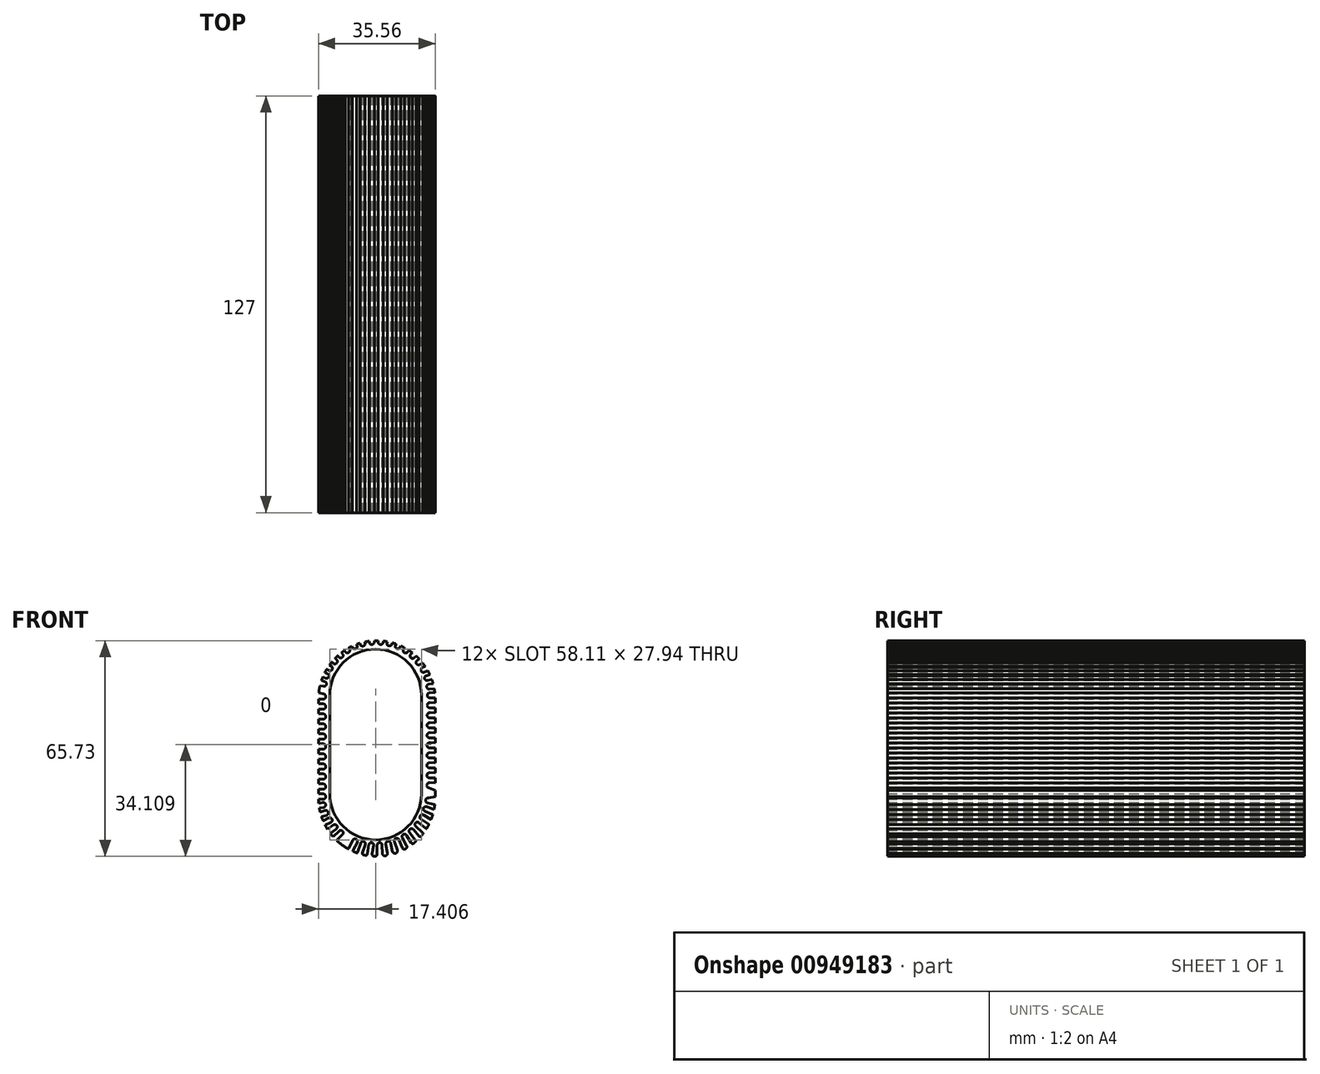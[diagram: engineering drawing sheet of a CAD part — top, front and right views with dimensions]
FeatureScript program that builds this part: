
annotation { "Feature Type Name" : "Feature", "Feature Type Description" : "" }
export const myFeature = defineFeature(function(context is Context, id is Id, definition is map)
    precondition{}
    {
        {
            var Q0;
            Q0=qCreatedBy(makeId("Front.planeOp"),FACE);
            var sketch = newSketch(context, id + "F0", { "sketchPlane" : qUnion([Q0])});
            skLineSegment(sketch, "E0", {"start": v(-13.83, 27.75) * mm, "end": v(-13.83, -2.42) * mm});
            skArc(sketch, "E1", {"start": v(14.1, 27.75) * mm, "mid": v(0.14, 41.72) * mm, "end": v(-13.83, 27.75) * mm});
            skLineSegment(sketch, "E2", {"start": v(14.1, 27.75) * mm, "end": v(14.1, -2.42) * mm});
            skArc(sketch, "E3", {"start": v(-13.83, -2.42) * mm, "mid": v(0.14, -16.39) * mm, "end": v(14.1, -2.42) * mm});
            skLineSegment(sketch, "E4", {"start": v(-0.26, 43.88) * mm, "end": v(-0.26, 46.62) * mm});
            skArc(sketch, "E5", {"start": v(1.27, 46.62) * mm, "mid": v(0.5, 47.38) * mm, "end": v(-0.26, 46.62) * mm});
            skArc(sketch, "E6", {"start": v(-1.78, 43.88) * mm, "mid": v(-1.02, 43.11) * mm, "end": v(-0.26, 43.88) * mm});
            skLineSegment(sketch, "E7", {"start": v(10.26, 54.84) * mm, "end": v(11.29, 54.45) * mm});
            skLineSegment(sketch, "E8", {"start": v(15.28, 62.77) * mm, "end": v(24.92, 59.85) * mm});
            skLineSegment(sketch, "E9", {"start": v(27, 48.57) * mm, "end": v(25.56, 56.37) * mm});
            skLineSegment(sketch, "E10", {"start": v(25.56, 56.37) * mm, "end": v(8.9, 53.3) * mm});
            skLineSegment(sketch, "E11", {"start": v(15.28, 62.77) * mm, "end": v(24.38, 62.77) * mm});
            skLineSegment(sketch, "E12.trimOffspring", {"start": v(24.92, 59.85) * mm, "end": v(24.38, 62.77) * mm});
            skArc(sketch, "E13.1.0", {"start": v(0.93, 44) * mm, "mid": v(1.56, 43.13) * mm, "end": v(2.43, 43.75) * mm});
            skLineSegment(sketch, "E13.1.1", {"start": v(2.43, 43.75) * mm, "end": v(2.89, 46.46) * mm});
            skArc(sketch, "E13.1.2", {"start": v(4.39, 46.21) * mm, "mid": v(3.76, 47.09) * mm, "end": v(2.89, 46.46) * mm});
            skArc(sketch, "E13.2.0", {"start": v(3.62, 43.69) * mm, "mid": v(4.1, 42.72) * mm, "end": v(5.07, 43.2) * mm});
            skLineSegment(sketch, "E13.2.1", {"start": v(5.07, 43.2) * mm, "end": v(5.96, 45.79) * mm});
            skArc(sketch, "E13.2.2", {"start": v(7.4, 45.3) * mm, "mid": v(6.92, 46.26) * mm, "end": v(5.96, 45.79) * mm});
            skArc(sketch, "E13.3.0", {"start": v(6.23, 42.93) * mm, "mid": v(6.54, 41.9) * mm, "end": v(7.57, 42.2) * mm});
            skLineSegment(sketch, "E13.3.1", {"start": v(7.57, 42.2) * mm, "end": v(8.88, 44.62) * mm});
            skArc(sketch, "E13.3.2", {"start": v(10.22, 43.9) * mm, "mid": v(9.9, 44.93) * mm, "end": v(8.88, 44.62) * mm});
            skArc(sketch, "E13.4.0", {"start": v(8.67, 41.75) * mm, "mid": v(8.8, 40.68) * mm, "end": v(9.87, 40.82) * mm});
            skLineSegment(sketch, "E13.4.1", {"start": v(9.87, 40.82) * mm, "end": v(11.56, 42.98) * mm});
            skArc(sketch, "E13.4.2", {"start": v(12.76, 42.05) * mm, "mid": v(12.63, 43.12) * mm, "end": v(11.56, 42.98) * mm});
            skArc(sketch, "E13.5.0", {"start": v(10.89, 40.19) * mm, "mid": v(10.84, 39.11) * mm, "end": v(11.92, 39.07) * mm});
            skLineSegment(sketch, "E13.5.1", {"start": v(11.92, 39.07) * mm, "end": v(13.94, 40.93) * mm});
            skArc(sketch, "E13.5.2", {"start": v(14.97, 39.8) * mm, "mid": v(15.02, 40.88) * mm, "end": v(13.94, 40.93) * mm});
            skArc(sketch, "E13.6.0", {"start": v(12.82, 38.28) * mm, "mid": v(12.6, 37.23) * mm, "end": v(13.65, 37) * mm});
            skLineSegment(sketch, "E13.6.1", {"start": v(13.65, 37) * mm, "end": v(15.95, 38.5) * mm});
            skArc(sketch, "E13.6.2", {"start": v(16.78, 37.23) * mm, "mid": v(17, 38.29) * mm, "end": v(15.95, 38.5) * mm});
            skArc(sketch, "E13.7.0", {"start": v(14.4, 36.09) * mm, "mid": v(14.02, 35.08) * mm, "end": v(15.02, 34.7) * mm});
            skLineSegment(sketch, "E13.7.1", {"start": v(15.02, 34.7) * mm, "end": v(17.54, 35.8) * mm});
            skArc(sketch, "E13.7.2", {"start": v(18.15, 34.4) * mm, "mid": v(18.54, 35.4) * mm, "end": v(17.54, 35.8) * mm});
            skArc(sketch, "E13.8.0", {"start": v(15.61, 33.66) * mm, "mid": v(15.06, 32.73) * mm, "end": v(15.99, 32.18) * mm});
            skLineSegment(sketch, "E13.8.1", {"start": v(15.99, 32.18) * mm, "end": v(18.65, 32.85) * mm});
            skArc(sketch, "E13.8.2", {"start": v(19.02, 31.38) * mm, "mid": v(19.58, 32.3) * mm, "end": v(18.65, 32.85) * mm});
            skArc(sketch, "E13.9.0", {"start": v(16.4, 31.06) * mm, "mid": v(15.7, 30.24) * mm, "end": v(16.53, 29.54) * mm});
            skLineSegment(sketch, "E13.9.1", {"start": v(16.53, 29.54) * mm, "end": v(19.27, 29.77) * mm});
            skArc(sketch, "E13.9.2", {"start": v(19.35, 28.34) * mm, "mid": v(19.81, 29.08) * mm, "end": v(19.27, 29.77) * mm});
            skArc(sketch, "E13.10.0", {"start": v(16.7, 28.46) * mm, "mid": v(15.87, 27.7) * mm, "end": v(16.63, 26.85) * mm});
            skLineSegment(sketch, "E13.10.1", {"start": v(16.49, -0.58) * mm, "end": v(18.8, -1.49) * mm});
            skArc(sketch, "E13.10.2", {"start": v(19.12, -3.13) * mm, "mid": v(19.52, -2.2) * mm, "end": v(18.8, -1.49) * mm});
            skArc(sketch, "E13.11.0", {"start": v(16.3, -3.65) * mm, "mid": v(15.38, -4.2) * mm, "end": v(15.93, -5.13) * mm});
            skLineSegment(sketch, "E13.11.1", {"start": v(15.93, -5.13) * mm, "end": v(18.6, -5.8) * mm});
            skArc(sketch, "E13.11.2", {"start": v(18.22, -7.28) * mm, "mid": v(19.15, -6.73) * mm, "end": v(18.6, -5.8) * mm});
            skArc(sketch, "E13.12.0", {"start": v(15.77, -6.3) * mm, "mid": v(14.76, -6.7) * mm, "end": v(15.16, -7.7) * mm});
            skLineSegment(sketch, "E13.12.1", {"start": v(15.16, -7.7) * mm, "end": v(17.67, -8.8) * mm});
            skArc(sketch, "E13.12.2", {"start": v(17.06, -10.2) * mm, "mid": v(18.06, -9.81) * mm, "end": v(17.67, -8.8) * mm});
            skArc(sketch, "E13.13.0", {"start": v(14.8, -8.84) * mm, "mid": v(13.74, -9.06) * mm, "end": v(13.96, -10.12) * mm});
            skLineSegment(sketch, "E13.13.1", {"start": v(13.96, -10.12) * mm, "end": v(16.26, -11.62) * mm});
            skArc(sketch, "E13.13.2", {"start": v(15.43, -12.9) * mm, "mid": v(16.48, -12.67) * mm, "end": v(16.26, -11.62) * mm});
            skArc(sketch, "E13.14.0", {"start": v(13.42, -11.18) * mm, "mid": v(12.35, -11.22) * mm, "end": v(12.4, -12.3) * mm});
            skLineSegment(sketch, "E13.14.1", {"start": v(12.4, -12.3) * mm, "end": v(14.41, -14.16) * mm});
            skArc(sketch, "E13.14.2", {"start": v(13.38, -15.28) * mm, "mid": v(14.46, -15.24) * mm, "end": v(14.41, -14.16) * mm});
            skArc(sketch, "E13.15.0", {"start": v(11.68, -13.26) * mm, "mid": v(10.61, -13.13) * mm, "end": v(10.48, -14.2) * mm});
            skLineSegment(sketch, "E13.15.1", {"start": v(10.48, -14.2) * mm, "end": v(12.17, -16.36) * mm});
            skArc(sketch, "E13.15.2", {"start": v(10.97, -17.3) * mm, "mid": v(12.03, -17.43) * mm, "end": v(12.17, -16.36) * mm});
            skArc(sketch, "E13.16.0", {"start": v(9.63, -15.03) * mm, "mid": v(8.6, -14.72) * mm, "end": v(8.28, -15.75) * mm});
            skLineSegment(sketch, "E13.16.1", {"start": v(8.28, -15.75) * mm, "end": v(9.6, -18.17) * mm});
            skArc(sketch, "E13.16.2", {"start": v(8.25, -18.9) * mm, "mid": v(9.28, -19.2) * mm, "end": v(9.6, -18.17) * mm});
            skArc(sketch, "E13.17.0", {"start": v(7.3, -16.43) * mm, "mid": v(6.34, -15.95) * mm, "end": v(5.86, -16.92) * mm});
            skLineSegment(sketch, "E13.17.1", {"start": v(5.86, -16.92) * mm, "end": v(6.75, -19.52) * mm});
            skArc(sketch, "E13.17.2", {"start": v(5.31, -20.01) * mm, "mid": v(6.28, -20.49) * mm, "end": v(6.75, -19.52) * mm});
            skArc(sketch, "E13.18.0", {"start": v(4.78, -17.43) * mm, "mid": v(3.9, -16.8) * mm, "end": v(3.28, -17.68) * mm});
            skLineSegment(sketch, "E13.18.1", {"start": v(3.28, -17.68) * mm, "end": v(3.73, -20.39) * mm});
            skArc(sketch, "E13.18.2", {"start": v(2.23, -20.64) * mm, "mid": v(3.1, -21.27) * mm, "end": v(3.73, -20.39) * mm});
            skArc(sketch, "E13.19.0", {"start": v(2.13, -18) * mm, "mid": v(1.37, -17.24) * mm, "end": v(0.6, -18) * mm});
            skLineSegment(sketch, "E13.19.1", {"start": v(0.6, -18) * mm, "end": v(0.6, -20.75) * mm});
            skArc(sketch, "E13.19.2", {"start": v(-0.92, -20.75) * mm, "mid": v(-0.15, -21.51) * mm, "end": v(0.6, -20.75) * mm});
            skPoint(sketch, "E13.center", {"position": v(0, -1.72) * mm});
            skLineSegment(sketch, "E14", {"start": v(1.27, 46.62) * mm, "end": v(0.93, 44) * mm});
            skLineSegment(sketch, "E15", {"start": v(4.39, 46.21) * mm, "end": v(3.62, 43.69) * mm});
            skLineSegment(sketch, "E16", {"start": v(7.4, 45.3) * mm, "end": v(6.23, 42.93) * mm});
            skLineSegment(sketch, "E17", {"start": v(10.22, 43.9) * mm, "end": v(8.67, 41.75) * mm});
            skLineSegment(sketch, "E18", {"start": v(12.76, 42.05) * mm, "end": v(10.89, 40.19) * mm});
            skLineSegment(sketch, "E19", {"start": v(14.97, 39.8) * mm, "end": v(12.82, 38.28) * mm});
            skLineSegment(sketch, "E20", {"start": v(16.78, 37.23) * mm, "end": v(14.4, 36.09) * mm});
            skLineSegment(sketch, "E21", {"start": v(18.15, 34.4) * mm, "end": v(15.61, 33.66) * mm});
            skLineSegment(sketch, "E22", {"start": v(19.02, 31.38) * mm, "end": v(16.4, 31.06) * mm});
            skLineSegment(sketch, "E23", {"start": v(19.35, 28.34) * mm, "end": v(16.7, 28.46) * mm});
            skLineSegment(sketch, "E24", {"start": v(19.12, -3.13) * mm, "end": v(16.3, -3.65) * mm});
            skLineSegment(sketch, "E25", {"start": v(18.22, -7.28) * mm, "end": v(15.77, -6.3) * mm});
            skLineSegment(sketch, "E26", {"start": v(17.06, -10.2) * mm, "end": v(14.8, -8.84) * mm});
            skLineSegment(sketch, "E27", {"start": v(15.43, -12.9) * mm, "end": v(13.42, -11.18) * mm});
            skLineSegment(sketch, "E28", {"start": v(13.38, -15.28) * mm, "end": v(11.68, -13.26) * mm});
            skLineSegment(sketch, "E29", {"start": v(10.97, -17.3) * mm, "end": v(9.63, -15.03) * mm});
            skLineSegment(sketch, "E30", {"start": v(8.25, -18.9) * mm, "end": v(7.3, -16.43) * mm});
            skLineSegment(sketch, "E31", {"start": v(5.31, -20.01) * mm, "end": v(4.78, -17.43) * mm});
            skLineSegment(sketch, "E32", {"start": v(2.23, -20.64) * mm, "end": v(2.13, -18) * mm});
            skArc(sketch, "E33.1.0", {"start": v(-3.86, -20.37) * mm, "mid": v(-3.23, -21.25) * mm, "end": v(-2.36, -20.61) * mm});
            skLineSegment(sketch, "E33.1.1", {"start": v(-1.93, -17.9) * mm, "end": v(-2.36, -20.61) * mm});
            skArc(sketch, "E33.1.2", {"start": v(-0.43, -18.14) * mm, "mid": v(-1.06, -17.26) * mm, "end": v(-1.93, -17.9) * mm});
            skArc(sketch, "E33.2.0", {"start": v(-6.72, -19.55) * mm, "mid": v(-6.23, -20.5) * mm, "end": v(-5.27, -20.01) * mm});
            skLineSegment(sketch, "E33.2.1", {"start": v(-4.42, -17.4) * mm, "end": v(-5.27, -20.01) * mm});
            skArc(sketch, "E33.2.2", {"start": v(-2.97, -17.87) * mm, "mid": v(-3.47, -16.91) * mm, "end": v(-4.42, -17.4) * mm});
            skArc(sketch, "E33.3.0", {"start": v(-9.4, -18.28) * mm, "mid": v(-9.07, -19.3) * mm, "end": v(-8.05, -18.97) * mm});
            skLineSegment(sketch, "E33.3.1", {"start": v(-6.81, -16.52) * mm, "end": v(-8.05, -18.97) * mm});
            skArc(sketch, "E33.3.2", {"start": v(-5.45, -17.21) * mm, "mid": v(-5.79, -16.19) * mm, "end": v(-6.81, -16.52) * mm});
            skArc(sketch, "E33.4.0", {"start": v(-11.87, -16.62) * mm, "mid": v(-11.7, -17.68) * mm, "end": v(-10.64, -17.51) * mm});
            skLineSegment(sketch, "E33.4.1", {"start": v(-9.03, -15.28) * mm, "end": v(-10.64, -17.51) * mm});
            skArc(sketch, "E33.4.2", {"start": v(-7.8, -16.17) * mm, "mid": v(-7.97, -15.11) * mm, "end": v(-9.03, -15.28) * mm});
            skArc(sketch, "E33.5.0", {"start": v(-14.04, -14.6) * mm, "mid": v(-14.04, -15.67) * mm, "end": v(-12.96, -15.66) * mm});
            skLineSegment(sketch, "E33.5.1", {"start": v(-11.03, -13.71) * mm, "end": v(-12.96, -15.66) * mm});
            skArc(sketch, "E33.5.2", {"start": v(-9.95, -14.79) * mm, "mid": v(-9.95, -13.7) * mm, "end": v(-11.03, -13.71) * mm});
            skArc(sketch, "E33.6.0", {"start": v(-15.88, -12.25) * mm, "mid": v(-16.04, -13.32) * mm, "end": v(-14.97, -13.48) * mm});
            skLineSegment(sketch, "E33.6.1", {"start": v(-12.76, -11.85) * mm, "end": v(-14.97, -13.48) * mm});
            skArc(sketch, "E33.6.2", {"start": v(-11.86, -13.08) * mm, "mid": v(-11.7, -12.01) * mm, "end": v(-12.76, -11.85) * mm});
            skArc(sketch, "E33.7.0", {"start": v(-17.32, -9.65) * mm, "mid": v(-17.65, -10.68) * mm, "end": v(-16.62, -11) * mm});
            skLineSegment(sketch, "E33.7.1", {"start": v(-14.18, -9.74) * mm, "end": v(-16.62, -11) * mm});
            skArc(sketch, "E33.7.2", {"start": v(-13.48, -11.1) * mm, "mid": v(-13.15, -10.07) * mm, "end": v(-14.18, -9.74) * mm});
            skArc(sketch, "E33.8.0", {"start": v(-18.34, -6.86) * mm, "mid": v(-18.83, -7.83) * mm, "end": v(-17.86, -8.3) * mm});
            skLineSegment(sketch, "E33.8.1", {"start": v(-15.26, -7.44) * mm, "end": v(-17.86, -8.3) * mm});
            skArc(sketch, "E33.8.2", {"start": v(-14.78, -8.89) * mm, "mid": v(-14.3, -7.92) * mm, "end": v(-15.26, -7.44) * mm});
            skArc(sketch, "E33.9.0", {"start": v(-18.8, -3.93) * mm, "mid": v(-19.44, -4.75) * mm, "end": v(-18.67, -5.45) * mm});
            skLineSegment(sketch, "E33.9.1", {"start": v(-15.96, -5) * mm, "end": v(-18.67, -5.45) * mm});
            skArc(sketch, "E33.9.2", {"start": v(-15.71, -6.5) * mm, "mid": v(-15.08, -5.62) * mm, "end": v(-15.96, -5) * mm});
            skLineSegment(sketch, "E33.10.1", {"start": v(-15.92, -2.38) * mm, "end": v(-18.67, -2.4) * mm});
            skArc(sketch, "E33.10.2", {"start": v(-16.18, -3.99) * mm, "mid": v(-15.05, -3.34) * mm, "end": v(-15.92, -2.38) * mm});
            skArc(sketch, "E33.11.0", {"start": v(-18.7, 30.65) * mm, "mid": v(-19.42, 29.87) * mm, "end": v(-18.9, 28.94) * mm});
            skLineSegment(sketch, "E33.11.1", {"start": v(-15.92, 28.1) * mm, "end": v(-18.9, 28.94) * mm});
            skArc(sketch, "E33.12.0", {"start": v(-17.54, 34.15) * mm, "mid": v(-18.5, 33.65) * mm, "end": v(-18, 32.7) * mm});
            skLineSegment(sketch, "E33.12.1", {"start": v(-15.37, 31.87) * mm, "end": v(-18, 32.7) * mm});
            skArc(sketch, "E33.12.2", {"start": v(-15.82, 30.42) * mm, "mid": v(-14.87, 30.92) * mm, "end": v(-15.37, 31.87) * mm});
            skArc(sketch, "E33.13.0", {"start": v(-16.3, 36.85) * mm, "mid": v(-17.32, 36.5) * mm, "end": v(-16.97, 35.48) * mm});
            skLineSegment(sketch, "E33.13.1", {"start": v(-14.51, 34.27) * mm, "end": v(-16.97, 35.48) * mm});
            skArc(sketch, "E33.13.2", {"start": v(-15.19, 32.9) * mm, "mid": v(-14.17, 33.25) * mm, "end": v(-14.51, 34.27) * mm});
            skArc(sketch, "E33.14.0", {"start": v(-14.66, 39.33) * mm, "mid": v(-15.72, 39.14) * mm, "end": v(-15.54, 38.08) * mm});
            skLineSegment(sketch, "E33.14.1", {"start": v(-13.3, 36.5) * mm, "end": v(-15.54, 38.08) * mm});
            skArc(sketch, "E33.14.2", {"start": v(-14.17, 35.25) * mm, "mid": v(-13.11, 35.43) * mm, "end": v(-13.3, 36.5) * mm});
            skArc(sketch, "E33.15.0", {"start": v(-12.65, 41.52) * mm, "mid": v(-13.73, 41.5) * mm, "end": v(-13.71, 40.43) * mm});
            skLineSegment(sketch, "E33.15.1", {"start": v(-11.74, 38.51) * mm, "end": v(-13.71, 40.43) * mm});
            skArc(sketch, "E33.15.2", {"start": v(-12.8, 37.42) * mm, "mid": v(-11.73, 37.43) * mm, "end": v(-11.74, 38.51) * mm});
            skArc(sketch, "E33.16.0", {"start": v(-10.32, 43.37) * mm, "mid": v(-11.4, 43.52) * mm, "end": v(-11.54, 42.46) * mm});
            skLineSegment(sketch, "E33.16.1", {"start": v(-9.9, 40.26) * mm, "end": v(-11.54, 42.46) * mm});
            skArc(sketch, "E33.16.2", {"start": v(-11.12, 39.35) * mm, "mid": v(-10.05, 39.2) * mm, "end": v(-9.9, 40.26) * mm});
            skArc(sketch, "E33.17.0", {"start": v(-7.74, 44.84) * mm, "mid": v(-8.77, 45.16) * mm, "end": v(-9.09, 44.13) * mm});
            skLineSegment(sketch, "E33.17.1", {"start": v(-7.8, 41.7) * mm, "end": v(-9.09, 44.13) * mm});
            skArc(sketch, "E33.17.2", {"start": v(-9.15, 40.99) * mm, "mid": v(-8.12, 40.67) * mm, "end": v(-7.8, 41.7) * mm});
            skArc(sketch, "E33.18.0", {"start": v(-4.96, 45.89) * mm, "mid": v(-5.93, 46.36) * mm, "end": v(-6.4, 45.4) * mm});
            skLineSegment(sketch, "E33.18.1", {"start": v(-5.5, 42.8) * mm, "end": v(-6.4, 45.4) * mm});
            skArc(sketch, "E33.18.2", {"start": v(-6.95, 42.3) * mm, "mid": v(-5.98, 41.83) * mm, "end": v(-5.5, 42.8) * mm});
            skArc(sketch, "E33.19.0", {"start": v(-2.05, 46.5) * mm, "mid": v(-2.93, 47.11) * mm, "end": v(-3.55, 46.23) * mm});
            skLineSegment(sketch, "E33.19.1", {"start": v(-3.07, 43.52) * mm, "end": v(-3.55, 46.23) * mm});
            skArc(sketch, "E33.19.2", {"start": v(-4.57, 43.26) * mm, "mid": v(-3.7, 42.64) * mm, "end": v(-3.07, 43.52) * mm});
            skLineSegment(sketch, "E34", {"start": v(-0.92, -20.75) * mm, "end": v(-0.43, -18.14) * mm});
            skLineSegment(sketch, "E35", {"start": v(-3.86, -20.37) * mm, "end": v(-2.97, -17.87) * mm});
            skLineSegment(sketch, "E36", {"start": v(-6.72, -19.55) * mm, "end": v(-5.45, -17.21) * mm});
            skLineSegment(sketch, "E37", {"start": v(-9.4, -18.22) * mm, "end": v(-7.8, -16.17) * mm});
            skLineSegment(sketch, "E38", {"start": v(-11.87, -16.62) * mm, "end": v(-9.95, -14.79) * mm});
            skLineSegment(sketch, "E39", {"start": v(-14.04, -14.6) * mm, "end": v(-11.86, -13.08) * mm});
            skLineSegment(sketch, "E40", {"start": v(-15.86, -12.18) * mm, "end": v(-13.48, -11.1) * mm});
            skLineSegment(sketch, "E41", {"start": v(-17.32, -9.65) * mm, "end": v(-14.78, -8.89) * mm});
            skLineSegment(sketch, "E42", {"start": v(-18.34, -6.86) * mm, "end": v(-15.71, -6.5) * mm});
            skLineSegment(sketch, "E43", {"start": v(-18.8, -3.93) * mm, "end": v(-16.18, -3.99) * mm});
            skLineSegment(sketch, "E44", {"start": v(-18.7, 30.65) * mm, "end": v(-15.82, 30.42) * mm});
            skLineSegment(sketch, "E45", {"start": v(-17.54, 34.15) * mm, "end": v(-15.19, 32.9) * mm});
            skLineSegment(sketch, "E46", {"start": v(-16.3, 36.85) * mm, "end": v(-14.17, 35.25) * mm});
            skLineSegment(sketch, "E47", {"start": v(-14.66, 39.33) * mm, "end": v(-12.8, 37.42) * mm});
            skLineSegment(sketch, "E48", {"start": v(-12.65, 41.52) * mm, "end": v(-11.12, 39.35) * mm});
            skLineSegment(sketch, "E49", {"start": v(-10.32, 43.37) * mm, "end": v(-9.15, 40.99) * mm});
            skLineSegment(sketch, "E50", {"start": v(-7.74, 44.84) * mm, "end": v(-6.95, 42.3) * mm});
            skLineSegment(sketch, "E51", {"start": v(-4.96, 45.89) * mm, "end": v(-4.57, 43.26) * mm});
            skLineSegment(sketch, "E52", {"start": v(-2.05, 46.5) * mm, "end": v(-1.78, 43.88) * mm});
            skLineSegment(sketch, "E53.0.1.0", {"start": v(-15.92, 0.67) * mm, "end": v(-18.67, 0.65) * mm});
            skArc(sketch, "E53.0.1.1", {"start": v(-16.18, -0.94) * mm, "mid": v(-15.05, -0.29) * mm, "end": v(-15.92, 0.67) * mm});
            skLineSegment(sketch, "E53.0.1.2", {"start": v(-18.8, -0.89) * mm, "end": v(-16.18, -0.94) * mm});
            skArc(sketch, "E53.0.1.3", {"start": v(-18.8, -0.89) * mm, "mid": v(-19.44, -1.7) * mm, "end": v(-18.67, -2.4) * mm});
            skLineSegment(sketch, "E53.0.2.0", {"start": v(-15.92, 3.72) * mm, "end": v(-18.67, 3.7) * mm});
            skArc(sketch, "E53.0.2.1", {"start": v(-16.18, 2.1) * mm, "mid": v(-15.05, 2.76) * mm, "end": v(-15.92, 3.72) * mm});
            skLineSegment(sketch, "E53.0.2.2", {"start": v(-18.8, 2.16) * mm, "end": v(-16.18, 2.1) * mm});
            skArc(sketch, "E53.0.2.3", {"start": v(-18.8, 2.16) * mm, "mid": v(-19.44, 1.34) * mm, "end": v(-18.67, 0.65) * mm});
            skLineSegment(sketch, "E53.0.3.0", {"start": v(-15.92, 6.77) * mm, "end": v(-18.67, 6.74) * mm});
            skArc(sketch, "E53.0.3.1", {"start": v(-16.18, 5.16) * mm, "mid": v(-15.05, 5.8) * mm, "end": v(-15.92, 6.77) * mm});
            skLineSegment(sketch, "E53.0.3.2", {"start": v(-18.8, 5.2) * mm, "end": v(-16.18, 5.16) * mm});
            skArc(sketch, "E53.0.3.3", {"start": v(-18.8, 5.2) * mm, "mid": v(-19.44, 4.4) * mm, "end": v(-18.67, 3.7) * mm});
            skLineSegment(sketch, "E53.0.4.0", {"start": v(-15.92, 9.82) * mm, "end": v(-18.67, 9.8) * mm});
            skArc(sketch, "E53.0.4.1", {"start": v(-16.18, 8.2) * mm, "mid": v(-15.05, 8.86) * mm, "end": v(-15.92, 9.82) * mm});
            skLineSegment(sketch, "E53.0.4.2", {"start": v(-18.8, 8.26) * mm, "end": v(-16.18, 8.2) * mm});
            skArc(sketch, "E53.0.4.3", {"start": v(-18.8, 8.26) * mm, "mid": v(-19.44, 7.44) * mm, "end": v(-18.67, 6.74) * mm});
            skLineSegment(sketch, "E53.0.5.0", {"start": v(-15.92, 12.86) * mm, "end": v(-18.67, 12.84) * mm});
            skArc(sketch, "E53.0.5.1", {"start": v(-16.18, 11.25) * mm, "mid": v(-15.05, 11.9) * mm, "end": v(-15.92, 12.86) * mm});
            skLineSegment(sketch, "E53.0.5.2", {"start": v(-18.8, 11.3) * mm, "end": v(-16.18, 11.25) * mm});
            skArc(sketch, "E53.0.5.3", {"start": v(-18.8, 11.3) * mm, "mid": v(-19.44, 10.49) * mm, "end": v(-18.67, 9.8) * mm});
            skLineSegment(sketch, "E53.0.6.0", {"start": v(-15.92, 15.91) * mm, "end": v(-18.67, 15.89) * mm});
            skArc(sketch, "E53.0.6.1", {"start": v(-16.18, 14.3) * mm, "mid": v(-15.05, 14.95) * mm, "end": v(-15.92, 15.91) * mm});
            skLineSegment(sketch, "E53.0.6.2", {"start": v(-18.8, 14.35) * mm, "end": v(-16.18, 14.3) * mm});
            skArc(sketch, "E53.0.6.3", {"start": v(-18.8, 14.35) * mm, "mid": v(-19.44, 13.54) * mm, "end": v(-18.67, 12.84) * mm});
            skLineSegment(sketch, "E53.0.7.0", {"start": v(-15.92, 18.96) * mm, "end": v(-18.67, 18.94) * mm});
            skArc(sketch, "E53.0.7.1", {"start": v(-16.18, 17.35) * mm, "mid": v(-15.05, 18) * mm, "end": v(-15.92, 18.96) * mm});
            skLineSegment(sketch, "E53.0.7.2", {"start": v(-18.8, 17.4) * mm, "end": v(-16.18, 17.35) * mm});
            skArc(sketch, "E53.0.7.3", {"start": v(-18.8, 17.4) * mm, "mid": v(-19.44, 16.58) * mm, "end": v(-18.67, 15.89) * mm});
            skLineSegment(sketch, "E53.0.8.0", {"start": v(-15.92, 22) * mm, "end": v(-18.67, 21.98) * mm});
            skArc(sketch, "E53.0.8.1", {"start": v(-16.18, 20.4) * mm, "mid": v(-15.05, 21.05) * mm, "end": v(-15.92, 22) * mm});
            skLineSegment(sketch, "E53.0.8.2", {"start": v(-18.8, 20.45) * mm, "end": v(-16.18, 20.4) * mm});
            skArc(sketch, "E53.0.8.3", {"start": v(-18.8, 20.45) * mm, "mid": v(-19.44, 19.63) * mm, "end": v(-18.67, 18.94) * mm});
            skLineSegment(sketch, "E53.0.9.0", {"start": v(-15.92, 25.06) * mm, "end": v(-18.67, 25.03) * mm});
            skArc(sketch, "E53.0.9.1", {"start": v(-16.18, 23.45) * mm, "mid": v(-15.05, 24.1) * mm, "end": v(-15.92, 25.06) * mm});
            skLineSegment(sketch, "E53.0.9.2", {"start": v(-18.8, 23.5) * mm, "end": v(-16.18, 23.45) * mm});
            skArc(sketch, "E53.0.9.3", {"start": v(-18.8, 23.5) * mm, "mid": v(-19.44, 22.68) * mm, "end": v(-18.67, 21.98) * mm});
            skArc(sketch, "E53.0.10.1", {"start": v(-16.18, 26.5) * mm, "mid": v(-15.05, 27.14) * mm, "end": v(-15.92, 28.1) * mm});
            skLineSegment(sketch, "E53.0.10.2", {"start": v(-18.8, 26.55) * mm, "end": v(-16.18, 26.5) * mm});
            skArc(sketch, "E53.0.10.3", {"start": v(-18.8, 26.55) * mm, "mid": v(-19.44, 25.73) * mm, "end": v(-18.67, 25.03) * mm});
            skLineSegment(sketch, "E53.direction2", {"start": v(-18.67, -5.45) * mm, "end": v(-18.67, -2.4) * mm, "construction": true});
            skLineSegment(sketch, "E54", {"start": v(16.63, 26.85) * mm, "end": v(19.33, 26.85) * mm});
            skArc(sketch, "E55", {"start": v(19.33, 25.29) * mm, "mid": v(20.11, 26.07) * mm, "end": v(19.33, 26.85) * mm});
            skArc(sketch, "E56.0.1.0", {"start": v(16.69, 25.41) * mm, "mid": v(15.85, 24.65) * mm, "end": v(16.61, 23.8) * mm});
            skLineSegment(sketch, "E56.0.1.1", {"start": v(16.61, 23.8) * mm, "end": v(19.32, 23.8) * mm});
            skArc(sketch, "E56.0.1.2", {"start": v(19.32, 22.24) * mm, "mid": v(20.1, 23.02) * mm, "end": v(19.32, 23.8) * mm});
            skLineSegment(sketch, "E56.0.1.3", {"start": v(19.33, 25.29) * mm, "end": v(16.69, 25.41) * mm});
            skArc(sketch, "E56.0.2.0", {"start": v(16.67, 22.36) * mm, "mid": v(15.83, 21.6) * mm, "end": v(16.6, 20.76) * mm});
            skLineSegment(sketch, "E56.0.2.1", {"start": v(16.6, 20.76) * mm, "end": v(19.3, 20.76) * mm});
            skArc(sketch, "E56.0.2.2", {"start": v(19.3, 19.2) * mm, "mid": v(20.08, 19.98) * mm, "end": v(19.3, 20.76) * mm});
            skLineSegment(sketch, "E56.0.2.3", {"start": v(19.32, 22.24) * mm, "end": v(16.67, 22.36) * mm});
            skArc(sketch, "E56.0.3.0", {"start": v(16.66, 19.32) * mm, "mid": v(15.82, 18.55) * mm, "end": v(16.58, 17.7) * mm});
            skLineSegment(sketch, "E56.0.3.1", {"start": v(16.58, 17.7) * mm, "end": v(19.28, 17.7) * mm});
            skArc(sketch, "E56.0.3.2", {"start": v(19.28, 16.15) * mm, "mid": v(20.07, 16.93) * mm, "end": v(19.28, 17.7) * mm});
            skLineSegment(sketch, "E56.0.3.3", {"start": v(19.3, 19.2) * mm, "end": v(16.66, 19.32) * mm});
            skArc(sketch, "E56.0.4.0", {"start": v(16.64, 16.27) * mm, "mid": v(15.8, 15.5) * mm, "end": v(16.57, 14.66) * mm});
            skLineSegment(sketch, "E56.0.4.1", {"start": v(16.57, 14.66) * mm, "end": v(19.27, 14.66) * mm});
            skArc(sketch, "E56.0.4.2", {"start": v(19.27, 13.1) * mm, "mid": v(20.05, 13.88) * mm, "end": v(19.27, 14.66) * mm});
            skLineSegment(sketch, "E56.0.4.3", {"start": v(19.28, 16.15) * mm, "end": v(16.64, 16.27) * mm});
            skArc(sketch, "E56.0.5.0", {"start": v(16.62, 13.22) * mm, "mid": v(15.78, 12.45) * mm, "end": v(16.55, 11.61) * mm});
            skLineSegment(sketch, "E56.0.5.1", {"start": v(16.55, 11.61) * mm, "end": v(19.25, 11.61) * mm});
            skArc(sketch, "E56.0.5.2", {"start": v(19.25, 10.05) * mm, "mid": v(20.03, 10.83) * mm, "end": v(19.25, 11.61) * mm});
            skLineSegment(sketch, "E56.0.5.3", {"start": v(19.27, 13.1) * mm, "end": v(16.62, 13.22) * mm});
            skArc(sketch, "E56.0.6.0", {"start": v(16.6, 10.17) * mm, "mid": v(15.77, 9.4) * mm, "end": v(16.53, 8.57) * mm});
            skLineSegment(sketch, "E56.0.6.1", {"start": v(16.53, 8.57) * mm, "end": v(19.24, 8.57) * mm});
            skArc(sketch, "E56.0.6.2", {"start": v(19.24, 7) * mm, "mid": v(20.02, 7.78) * mm, "end": v(19.24, 8.57) * mm});
            skLineSegment(sketch, "E56.0.6.3", {"start": v(19.25, 10.05) * mm, "end": v(16.6, 10.17) * mm});
            skArc(sketch, "E56.0.7.0", {"start": v(16.6, 7.12) * mm, "mid": v(15.75, 6.36) * mm, "end": v(16.52, 5.52) * mm});
            skLineSegment(sketch, "E56.0.7.1", {"start": v(16.52, 5.52) * mm, "end": v(19.22, 5.52) * mm});
            skArc(sketch, "E56.0.7.2", {"start": v(19.22, 3.95) * mm, "mid": v(20, 4.74) * mm, "end": v(19.22, 5.52) * mm});
            skLineSegment(sketch, "E56.0.7.3", {"start": v(19.24, 7) * mm, "end": v(16.6, 7.12) * mm});
            skArc(sketch, "E56.0.8.0", {"start": v(16.58, 4.08) * mm, "mid": v(15.74, 3.3) * mm, "end": v(16.5, 2.47) * mm});
            skLineSegment(sketch, "E56.0.8.1", {"start": v(16.5, 2.47) * mm, "end": v(19.2, 2.47) * mm});
            skArc(sketch, "E56.0.8.2", {"start": v(19.2, 0.9) * mm, "mid": v(19.99, 1.69) * mm, "end": v(19.2, 2.47) * mm});
            skLineSegment(sketch, "E56.0.8.3", {"start": v(19.22, 3.95) * mm, "end": v(16.58, 4.08) * mm});
            skArc(sketch, "E56.0.9.0", {"start": v(16.56, 1.03) * mm, "mid": v(15.72, 0.26) * mm, "end": v(16.49, -0.58) * mm});
            skLineSegment(sketch, "E56.0.9.3", {"start": v(19.2, 0.9) * mm, "end": v(16.56, 1.03) * mm});
            skLineSegment(sketch, "E56.direction2", {"start": v(16.63, 26.85) * mm, "end": v(16.61, 23.8) * mm, "construction": true});
            skArc(sketch, "E57.1.0.0", {"start": v(18.29, 26.5) * mm, "mid": v(0.5, 44.29) * mm, "end": v(-17.27, 26.5) * mm});
            skLineSegment(sketch, "E57.1.0.1", {"start": v(18.29, 26.5) * mm, "end": v(18.29, -3.66) * mm});
            skArc(sketch, "E57.1.0.2", {"start": v(-17.27, -3.66) * mm, "mid": v(0.5, -21.44) * mm, "end": v(18.29, -3.66) * mm});
            skLineSegment(sketch, "E58", {"start": v(-17.27, -3.66) * mm, "end": v(-17.27, 26.5) * mm});
            skSolve(sketch);
        }
        {
            var Q0;
            Q0=makeQuery(id+"F0.imprint","IMPRINT",FACE,{"disambiguationData":[TD([[makeQuery(id+"F0.imprint","IMPRINT",EDGE,{"derivedFrom":sQuery(id+"F0.wireOp",EDGE,"E0")}),-1.0]])]});
            var Q1;
            Q1=sQuery(id+"F0.wireOp",EDGE,"E2");
            var Q2;
            Q2=sQuery(id+"F0.wireOp",EDGE,"E1");
            var Q3;
            Q3=sQuery(id+"F0.wireOp",EDGE,"E0");
            var Q4;
            Q4=sQuery(id+"F0.wireOp",EDGE,"E3");
            extrude(context, id + "F1", {"entities" : qUnion([Q0]), "surfaceEntities" : qUnion([Q1, Q2, Q3, Q4]), "endBound" : BoundingType.SYMMETRIC, "depth" : 127 * mm, "offsetDistance" : 25.4 * mm});
        }
    });
